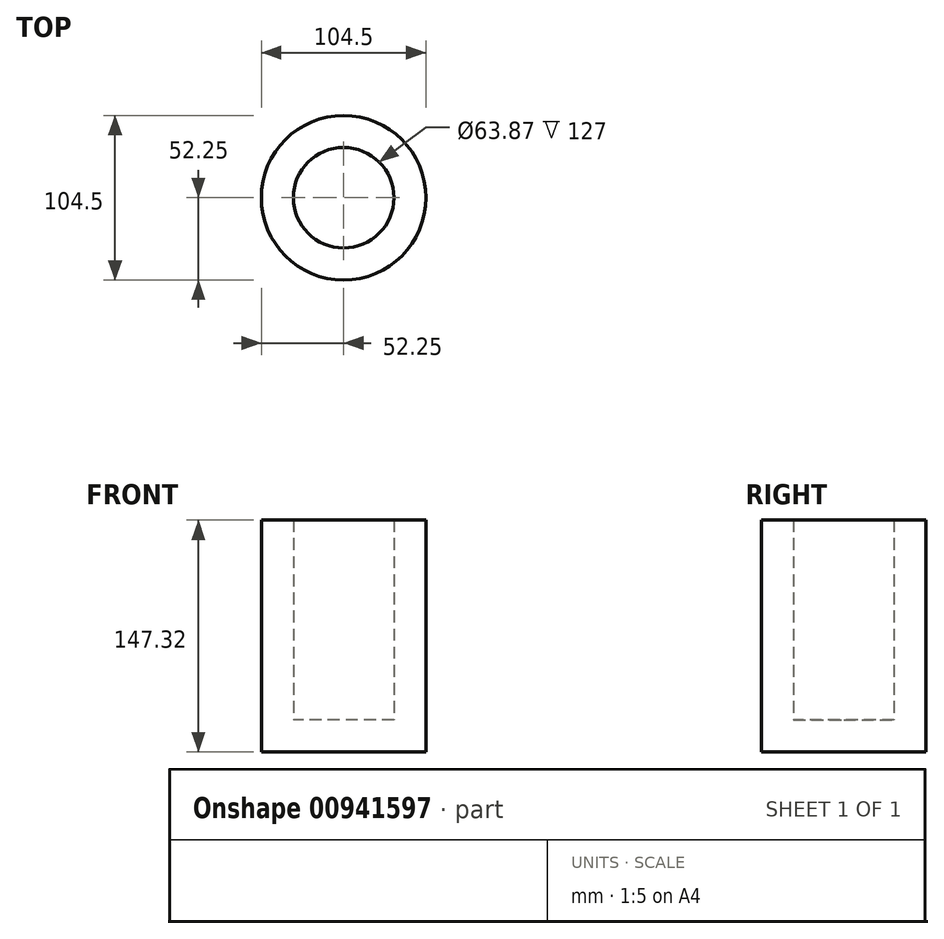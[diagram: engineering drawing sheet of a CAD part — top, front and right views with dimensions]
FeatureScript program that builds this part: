
annotation { "Feature Type Name" : "Feature", "Feature Type Description" : "" }
export const myFeature = defineFeature(function(context is Context, id is Id, definition is map)
    precondition{}
    {
        {
            var Q0;
            Q0=qCreatedBy(makeId("Top.planeOp"),FACE);
            var sketch = newSketch(context, id + "F0", { "sketchPlane" : qUnion([Q0])});
            skCircle(sketch, "E0", {"center": v(0, 0) * mm, "radius": 31.93 * mm});
            skSolve(sketch);
        }
        {
            var Q0;
            Q0 = qSketchRegion(id + "F0", true);
            extrude(context, id + "F1", {"entities" : qUnion([Q0]), "depth" : 127 * mm, "offsetDistance" : 25.4 * mm});
        }
        {
            var Q0;
            Q0=makeQuery(id+"F1.opExtrude","CAP_FACE",FACE,{"disambiguationData":[OSD([sQuery(id+"F0.wireOp",EDGE,"E0")])],"isStart":false});
            shell(context, id + "F2", {"entities" : qUnion([Q0]), "thickness" : 20.32 * mm, "oppositeDirection" : true});
        }
    });
